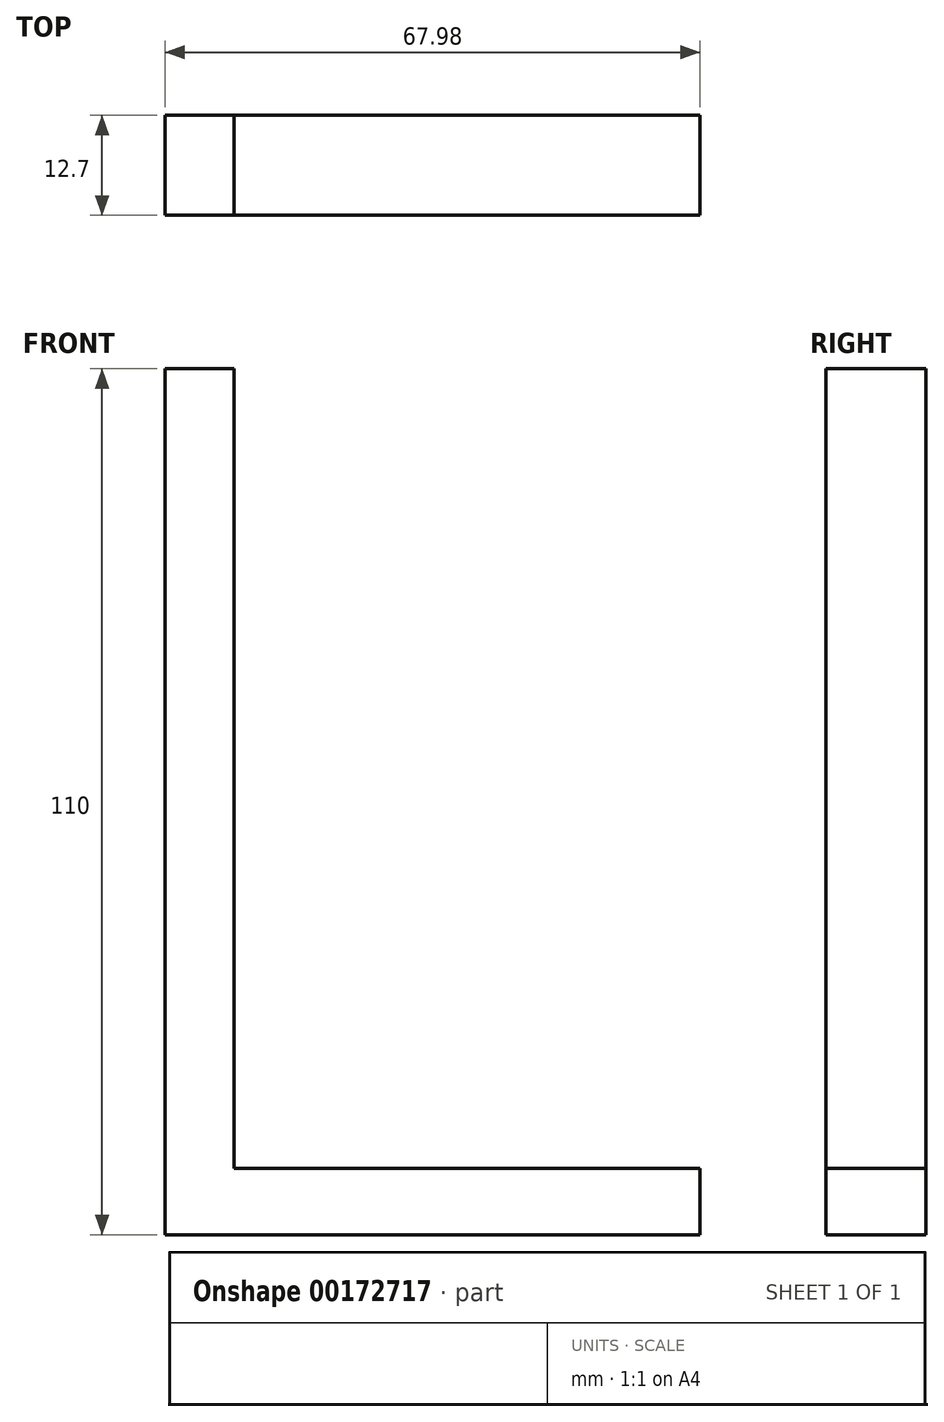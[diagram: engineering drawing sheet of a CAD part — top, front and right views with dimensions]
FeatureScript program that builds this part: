
annotation { "Feature Type Name" : "Feature", "Feature Type Description" : "" }
export const myFeature = defineFeature(function(context is Context, id is Id, definition is map)
    precondition{}
    {
        {
            var Q0;
            Q0=qCreatedBy(makeId("Front.planeOp"),FACE);
            var sketch = newSketch(context, id + "F0", { "sketchPlane" : qUnion([Q0])});
            skLineSegment(sketch, "E0.bottom", {"start": v(-49.46, 101.6) * mm, "end": v(-40.68, 101.6) * mm});
            skLineSegment(sketch, "E0.top", {"start": v(-49.46, 0) * mm, "end": v(-40.68, 0) * mm});
            skLineSegment(sketch, "E0.left", {"start": v(-49.46, 101.6) * mm, "end": v(-49.46, 0) * mm});
            skLineSegment(sketch, "E0.right", {"start": v(-40.68, 101.6) * mm, "end": v(-40.68, 0) * mm});
            skLineSegment(sketch, "E1.bottom", {"start": v(-49.46, 0) * mm, "end": v(18.52, 0) * mm});
            skLineSegment(sketch, "E1.top", {"start": v(-49.46, -8.4) * mm, "end": v(18.52, -8.4) * mm});
            skLineSegment(sketch, "E1.left", {"start": v(-49.46, 0) * mm, "end": v(-49.46, -8.4) * mm});
            skLineSegment(sketch, "E1.right", {"start": v(18.52, 0) * mm, "end": v(18.52, -8.4) * mm});
            skLineSegment(sketch, "E2.bottom", {"start": v(18.52, 0) * mm, "end": v(10.12, 0) * mm});
            skLineSegment(sketch, "E2.top", {"start": v(18.52, 101.6) * mm, "end": v(10.12, 101.6) * mm});
            skLineSegment(sketch, "E2.left", {"start": v(18.52, 0) * mm, "end": v(18.52, 101.6) * mm});
            skLineSegment(sketch, "E2.right", {"start": v(10.12, 0) * mm, "end": v(10.12, 101.6) * mm});
            skSolve(sketch);
        }
        {
            var Q0;
            Q0=makeQuery(id+"F0.imprint","IMPRINT",FACE,{"disambiguationData":[TD([[makeQuery(id+"F0.imprint","IMPRINT",EDGE,{"derivedFrom":sQuery(id+"F0.wireOp",EDGE,"E2.bottom")}),-1.0]])]});
            var Q1;
            Q1=makeQuery(id+"F0.imprint","IMPRINT",FACE,{"disambiguationData":[TD([[makeQuery(id+"F0.imprint","IMPRINT",EDGE,{"derivedFrom":sQuery(id+"F0.wireOp",EDGE,"E1.top")}),1.0]])]});
            var Q2;
            Q2=makeQuery(id+"F0.imprint","IMPRINT",FACE,{"disambiguationData":[TD([[makeQuery(id+"F0.imprint","IMPRINT",EDGE,{"derivedFrom":sQuery(id+"F0.wireOp",EDGE,"E0.bottom")}),-1.0]])]});
            extrude(context, id + "F1", {"entities" : qUnion([Q0, Q1, Q2]), "depth" : 12.7 * mm});
        }
    });
